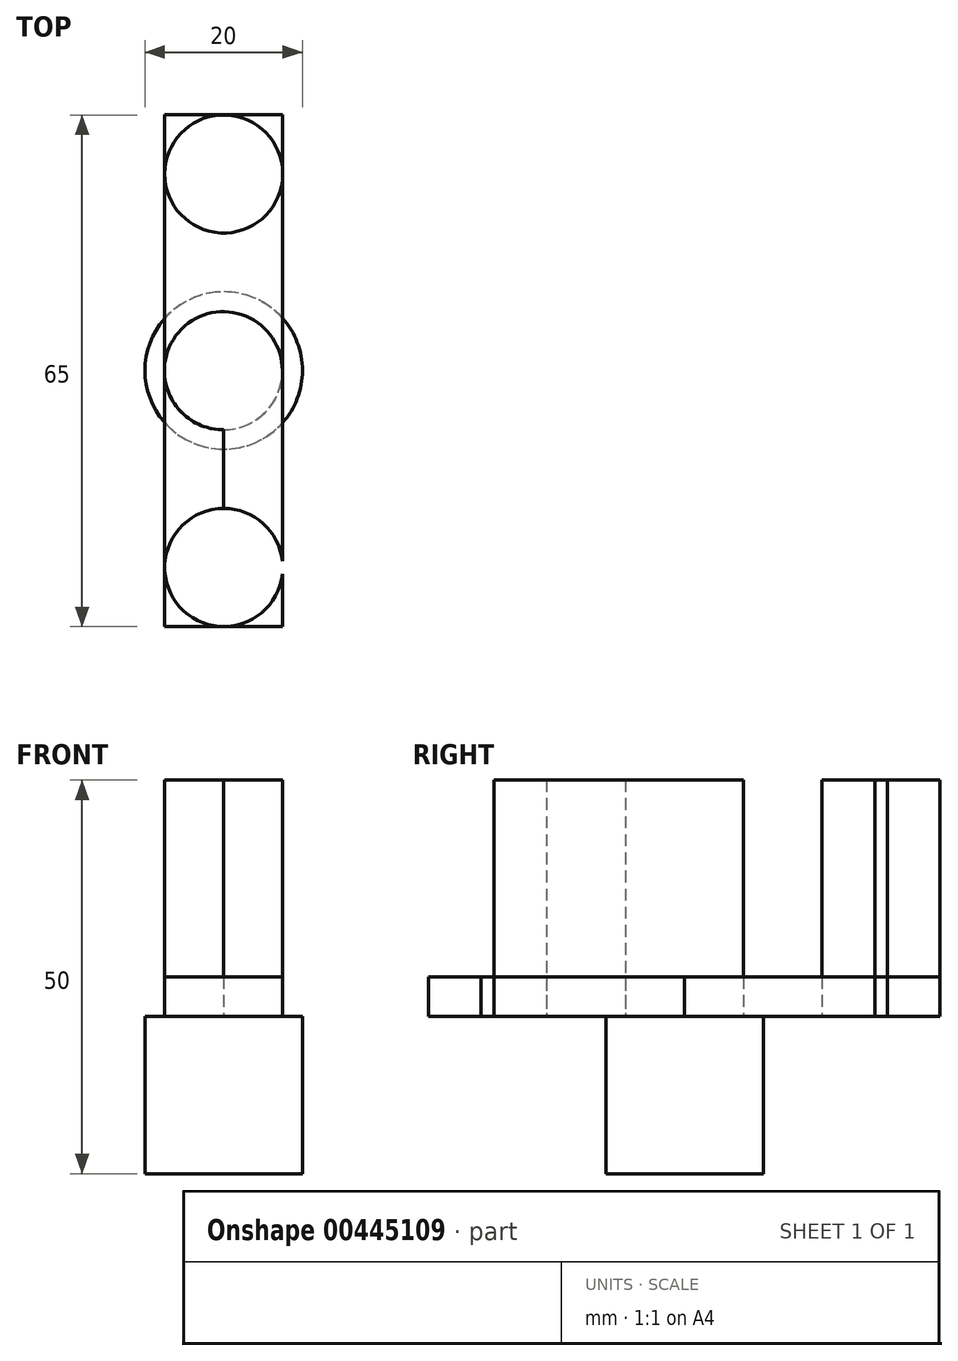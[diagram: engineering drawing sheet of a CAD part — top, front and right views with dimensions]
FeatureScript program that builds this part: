
annotation { "Feature Type Name" : "Feature", "Feature Type Description" : "" }
export const myFeature = defineFeature(function(context is Context, id is Id, definition is map)
    precondition{}
    {
        {
            var Q0;
            Q0=qCreatedBy(makeId("Top.planeOp"),FACE);
            var sketch = newSketch(context, id + "F0", { "sketchPlane" : qUnion([Q0])});
            skCircle(sketch, "E0", {"center": v(-0.04, -0.03) * mm, "radius": 7.5 * mm});
            skLineSegment(sketch, "E1", {"start": v(0, 7.47) * mm, "end": v(0, 24.97) * mm});
            skLineSegment(sketch, "E2", {"start": v(0, -7.53) * mm, "end": v(0, -25.03) * mm});
            skLineSegment(sketch, "E3.bottom", {"start": v(7.46, -32.53) * mm, "end": v(-7.54, -32.53) * mm});
            skLineSegment(sketch, "E3.top", {"start": v(7.46, 32.47) * mm, "end": v(-7.54, 32.47) * mm});
            skLineSegment(sketch, "E3.left", {"start": v(7.46, -32.53) * mm, "end": v(7.46, 32.47) * mm});
            skLineSegment(sketch, "E3.right", {"start": v(-7.54, -32.53) * mm, "end": v(-7.54, 32.47) * mm});
            skCircle(sketch, "E4", {"center": v(0, 24.97) * mm, "radius": 7.5 * mm});
            skCircle(sketch, "E5", {"center": v(0, -25.03) * mm, "radius": 7.5 * mm});
            skSolve(sketch);
        }
        {
            var Q0;
            Q0=qCreatedBy(makeId("Top.planeOp"),FACE);
            var sketch = newSketch(context, id + "F1", { "sketchPlane" : qUnion([Q0])});
            skCircle(sketch, "E6", {"center": v(0, 0) * mm, "radius": 10 * mm});
            skSolve(sketch);
        }
        {
            var Q0;
            {var subQ0=sQuery(id+"F0.wireOp",EDGE,"E5");var subQ1=sQuery(id+"F0.wireOp",EDGE,"E3.left");var subQ2=makeQuery(id+"F0.imprint","INTERSECT",VERTEX,{"disambiguationData":[OD(0.0)],"derivedFrom":[subQ1,subQ0]});Q0=makeQuery(id+"F0.imprint","IMPRINT",FACE,{"disambiguationData":[TD([[makeQuery(id+"F0.imprint","IMPRINT",EDGE,{"disambiguationData":[TD([[subQ2,-1.0]])],"derivedFrom":subQ1}),-1.0]])]});}
            var Q1;
            {var subQ0=sQuery(id+"F0.wireOp",EDGE,"E4");var subQ1=sQuery(id+"F0.wireOp",EDGE,"E3.left");var subQ2=makeQuery(id+"F0.imprint","INTERSECT",VERTEX,{"disambiguationData":[OD(0.0)],"derivedFrom":[subQ1,subQ0]});Q1=makeQuery(id+"F0.imprint","IMPRINT",FACE,{"disambiguationData":[TD([[makeQuery(id+"F0.imprint","IMPRINT",EDGE,{"disambiguationData":[TD([[subQ2,-1.0]])],"derivedFrom":subQ1}),-1.0]])]});}
            var Q2;
            {var subQ0=sQuery(id+"F0.wireOp",EDGE,"E1");var subQ1=sQuery(id+"F0.wireOp",EDGE,"E0");var subQ2=makeQuery(id+"F0.imprint","INTERSECT",VERTEX,{"derivedFrom":[subQ1,subQ0]});Q2=makeQuery(id+"F0.imprint","IMPRINT",FACE,{"disambiguationData":[TD([[makeQuery(id+"F0.imprint","IMPRINT",EDGE,{"disambiguationData":[TD([[subQ2,1.0]])],"derivedFrom":subQ1}),-1.0]])]});}
            var Q3;
            {var subQ1=sQuery(id+"F0.wireOp",EDGE,"E3.top");Q3=makeQuery(id+"F0.imprint","IMPRINT",FACE,{"disambiguationData":[TD([[makeQuery(id+"F0.imprint","IMPRINT",EDGE,{"derivedFrom":subQ1}),1.0]])]});}
            var Q4;
            {var subQ1=sQuery(id+"F0.wireOp",EDGE,"E3.bottom");Q4=makeQuery(id+"F0.imprint","IMPRINT",FACE,{"disambiguationData":[TD([[makeQuery(id+"F0.imprint","IMPRINT",EDGE,{"derivedFrom":subQ1}),-1.0]])]});}
            var Q5;
            {var subQ0=sQuery(id+"F0.wireOp",EDGE,"E2");var subQ1=sQuery(id+"F0.wireOp",EDGE,"E0");var subQ2=makeQuery(id+"F0.imprint","INTERSECT",VERTEX,{"derivedFrom":[subQ1,subQ0]});Q5=makeQuery(id+"F0.imprint","IMPRINT",FACE,{"disambiguationData":[TD([[makeQuery(id+"F0.imprint","IMPRINT",EDGE,{"disambiguationData":[TD([[subQ2,-1.0]])],"derivedFrom":subQ1}),-1.0]])]});}
            extrude(context, id + "F2", {"entities" : qUnion([Q0, Q1, Q2, Q3, Q4, Q5]), "depth" : 5 * mm});
        }
        {
            var Q0;
            {var subQ0=sQuery(id+"F0.wireOp",EDGE,"E4");var subQ1=sQuery(id+"F0.wireOp",EDGE,"E3.left");var subQ2=makeQuery(id+"F0.imprint","INTERSECT",VERTEX,{"disambiguationData":[OD(0.0)],"derivedFrom":[subQ1,subQ0]});Q0=makeQuery(id+"F0.imprint","IMPRINT",FACE,{"disambiguationData":[TD([[makeQuery(id+"F0.imprint","IMPRINT",EDGE,{"disambiguationData":[TD([[subQ2,-1.0]])],"derivedFrom":subQ1}),1.0]])]});}
            var Q1;
            {var subQ0=sQuery(id+"F0.wireOp",EDGE,"E0");var subQ1=makeQuery(id+"F0.imprint","INTERSECT",VERTEX,{"derivedFrom":[subQ0,sQuery(id+"F0.wireOp",EDGE,"E1")]});Q1=makeQuery(id+"F0.imprint","IMPRINT",FACE,{"disambiguationData":[TD([[makeQuery(id+"F0.imprint","IMPRINT",EDGE,{"disambiguationData":[TD([[subQ1,1.0]])],"derivedFrom":subQ0}),1.0]])]});}
            var Q2;
            {var subQ0=sQuery(id+"F0.wireOp",EDGE,"E5");var subQ1=sQuery(id+"F0.wireOp",EDGE,"E3.left");var subQ2=makeQuery(id+"F0.imprint","INTERSECT",VERTEX,{"disambiguationData":[OD(0.0)],"derivedFrom":[subQ1,subQ0]});Q2=makeQuery(id+"F0.imprint","IMPRINT",FACE,{"disambiguationData":[TD([[makeQuery(id+"F0.imprint","IMPRINT",EDGE,{"disambiguationData":[TD([[subQ2,-1.0]])],"derivedFrom":subQ1}),1.0]])]});}
            extrude(context, id + "F3", {"entities" : qUnion([Q0, Q1, Q2]), "depth" : 30 * mm});
        }
        {
            var Q0;
            Q0=makeQuery(id+"F1.imprint","IMPRINT",FACE,{"disambiguationData":[TD([[makeQuery(id+"F1.imprint","IMPRINT",EDGE,{"derivedFrom":sQuery(id+"F1.wireOp",EDGE,"E6")}),1.0]])]});
            extrude(context, id + "F4", {"entities" : qUnion([Q0]), "oppositeDirection" : true, "depth" : 20 * mm});
        }
    });
